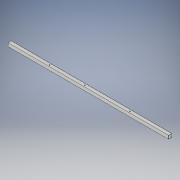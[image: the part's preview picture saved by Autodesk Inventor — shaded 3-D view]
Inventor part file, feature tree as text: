
AUTODESK INVENTOR PART (.ipt)
format: ipt  version: 2017 (Build 210142000, 142)  size: 115,200 bytes
history: native  units: in
note: dims shown in document units (in); Inventor stores cm internally (conversion verified against a paired STEP export)
features: extrude x2, sketch x2
ambient origin geometry x8: Origin, YZ Plane, XZ Plane, XY Plane, X Axis, Y Axis, Z Axis, Center Point
bodies: Solid1 (feature_tree)
feature tree (4):
  extrude  "Extrusion1"  Depth=1.0in
  extrude  "Extrusion3"  Depth=48.0in TaperAngle=0.0deg
  sketch  "Sketch1"  dims[d0=1.0in d1=1.0in]
  sketch  "Sketch3"  dims[d2=0.0625in d3=48.0in d4=0.0in d10=0.25in d11=12.0in d12=1.0in d13=0.0in d14=1.5in]
